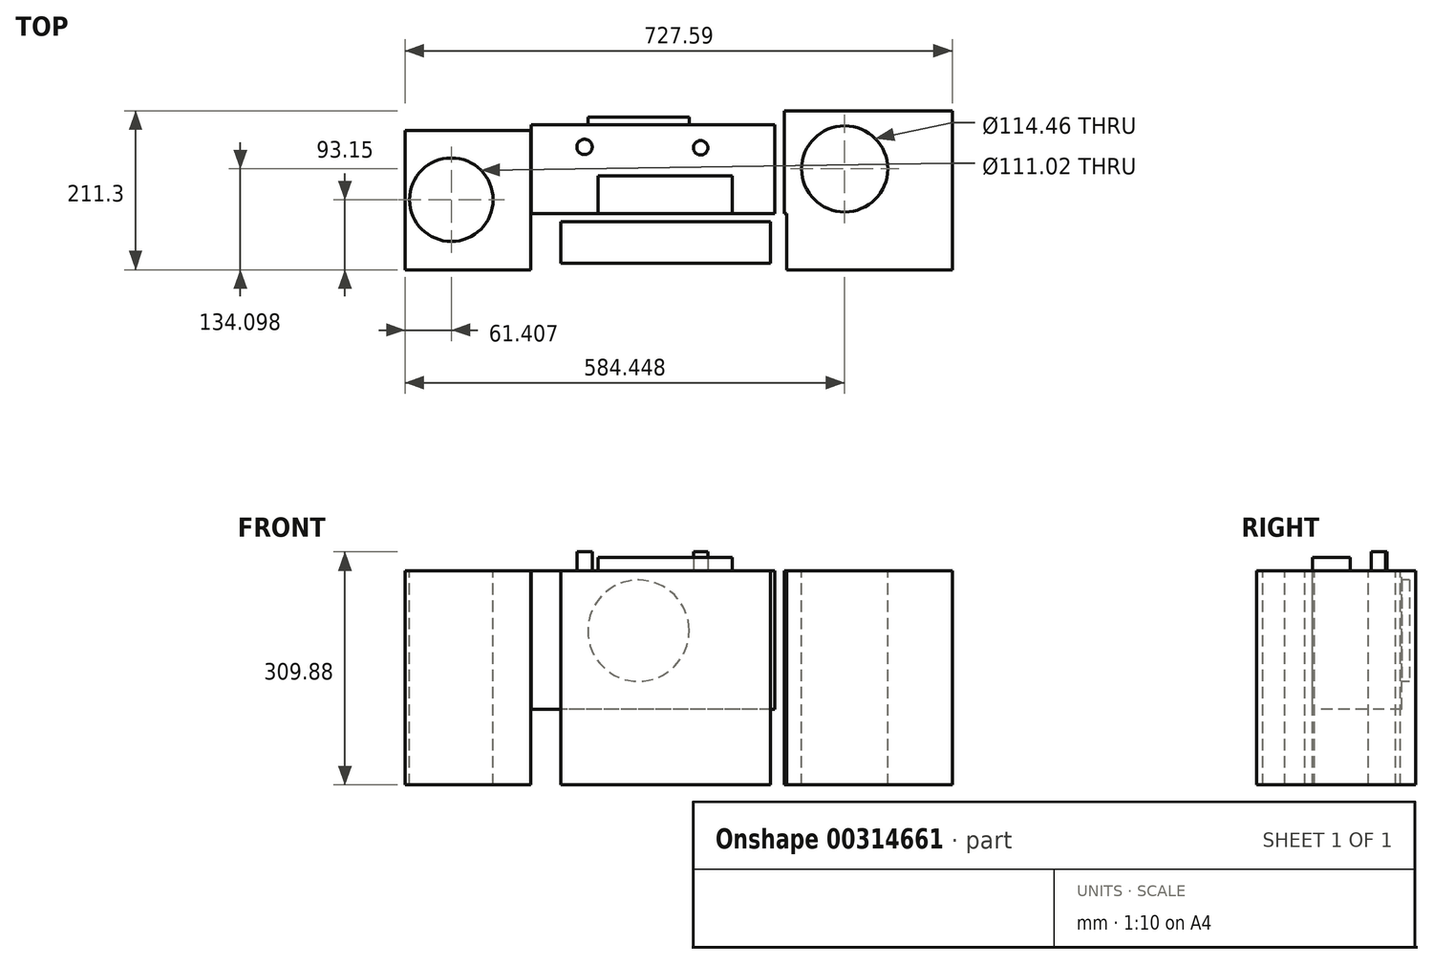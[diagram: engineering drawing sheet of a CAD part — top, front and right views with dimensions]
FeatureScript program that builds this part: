
annotation { "Feature Type Name" : "Feature", "Feature Type Description" : "" }
export const myFeature = defineFeature(function(context is Context, id is Id, definition is map)
    precondition{}
    {
        {
            var Q0;
            Q0=qCreatedBy(makeId("Top.planeOp"),FACE);
            var sketch = newSketch(context, id + "F0", { "sketchPlane" : qUnion([Q0])});
            skLineSegment(sketch, "E0.bottom", {"start": v(-134.95, 54.2) * mm, "end": v(69.6, 54.2) * mm});
            skLineSegment(sketch, "E0.top", {"start": v(-134.95, 26.65) * mm, "end": v(69.6, 26.65) * mm});
            skLineSegment(sketch, "E0.left", {"start": v(-134.95, 54.2) * mm, "end": v(-134.95, 26.65) * mm});
            skLineSegment(sketch, "E0.right", {"start": v(69.6, 54.2) * mm, "end": v(69.6, 26.65) * mm});
            skLineSegment(sketch, "E1.bottom", {"start": v(69.6, -77.72) * mm, "end": v(-134.95, -77.72) * mm});
            skLineSegment(sketch, "E1.top", {"start": v(69.6, 26.65) * mm, "end": v(-134.95, 26.65) * mm});
            skLineSegment(sketch, "E1.left", {"start": v(69.6, -77.72) * mm, "end": v(69.6, 26.65) * mm});
            skLineSegment(sketch, "E1.right", {"start": v(-134.95, -77.72) * mm, "end": v(-134.95, 26.65) * mm});
            skLineSegment(sketch, "E2.top", {"start": v(-134.95, 85.93) * mm, "end": v(69.6, 85.93) * mm});
            skLineSegment(sketch, "E2.left", {"start": v(-134.95, 54.2) * mm, "end": v(-134.95, 85.93) * mm});
            skLineSegment(sketch, "E2.right", {"start": v(69.6, 54.2) * mm, "end": v(69.6, 85.93) * mm});
            skSolve(sketch);
        }
        {
            var Q0;
            Q0=makeQuery(id+"F0.imprint","IMPRINT",FACE,{"disambiguationData":[TD([[makeQuery(id+"F0.imprint","IMPRINT",EDGE,{"derivedFrom":sQuery(id+"F0.wireOp",EDGE,"E0.bottom")}),1.0]])]});
            extrude(context, id + "F1", {"entities" : qUnion([Q0]), "depth" : 57.4 * mm});
        }
        {
            var Q0;
            Q0=makeQuery(id+"F1.opExtrude","CAP_FACE",FACE,{"disambiguationData":[OSD([sQuery(id+"F0.wireOp",EDGE,"E0.bottom"),sQuery(id+"F0.wireOp",EDGE,"E2.top"),sQuery(id+"F0.wireOp",EDGE,"E2.left"),sQuery(id+"F0.wireOp",EDGE,"E2.right")])],"isStart":false});
            var sketch = newSketch(context, id + "F2", { "sketchPlane" : qUnion([Q0])});
            skCircle(sketch, "E3", {"center": v(-110.98, 70.21) * mm, "radius": 10.18 * mm});
            skCircle(sketch, "E4", {"center": v(43.42, 69.05) * mm, "radius": 9.58 * mm});
            skSolve(sketch);
        }
        {
            var Q0;
            Q0 = qSketchRegion(id + "F2", true);
            extrude(context, id + "F3", {"entities" : qUnion([Q0]), "operationType" : NewBodyOperationType.ADD, "depth" : 25.4 * mm});
        }
        {
            var Q0;
            Q0=makeQuery(id+"F1.opExtrude","CAP_FACE",FACE,{"disambiguationData":[OSD([sQuery(id+"F0.wireOp",EDGE,"E0.bottom"),sQuery(id+"F0.wireOp",EDGE,"E2.top"),sQuery(id+"F0.wireOp",EDGE,"E2.left"),sQuery(id+"F0.wireOp",EDGE,"E2.right")])],"isStart":false});
            var sketch = newSketch(context, id + "F4", { "sketchPlane" : qUnion([Q0])});
            skLineSegment(sketch, "E5.bottom", {"start": v(142.11, 99.6) * mm, "end": v(-181.77, 99.6) * mm});
            skLineSegment(sketch, "E5.top", {"start": v(142.11, -18.76) * mm, "end": v(-181.77, -18.76) * mm});
            skLineSegment(sketch, "E5.left", {"start": v(142.11, 99.6) * mm, "end": v(142.11, -18.76) * mm});
            skLineSegment(sketch, "E5.right", {"start": v(-181.77, 99.6) * mm, "end": v(-181.77, -18.76) * mm});
            skSolve(sketch);
        }
        {
            var Q0;
            Q0 = qSketchRegion(id + "F4", true);
            extrude(context, id + "F5", {"entities" : qUnion([Q0]), "operationType" : NewBodyOperationType.ADD, "oppositeDirection" : true, "depth" : 183.9 * mm});
        }
        {
            var Q0;
            Q0=makeQuery(id+"F5.boolean.opBoolean","MERGE",FACE,{"derivedFrom":[makeQuery(id+"F1.opExtrude","CAP_FACE",FACE,{"disambiguationData":[OSD([sQuery(id+"F0.wireOp",EDGE,"E0.bottom"),sQuery(id+"F0.wireOp",EDGE,"E2.top"),sQuery(id+"F0.wireOp",EDGE,"E2.left"),sQuery(id+"F0.wireOp",EDGE,"E2.right")])],"isStart":false}),makeQuery(id+"F5.opExtrude","CAP_FACE",FACE,{"disambiguationData":[OSD([sQuery(id+"F4.wireOp",EDGE,"E5.bottom"),sQuery(id+"F4.wireOp",EDGE,"E5.top"),sQuery(id+"F4.wireOp",EDGE,"E5.left"),sQuery(id+"F4.wireOp",EDGE,"E5.right")])],"isStart":true})]});
            var sketch = newSketch(context, id + "F6", { "sketchPlane" : qUnion([Q0])});
            skLineSegment(sketch, "E6.bottom", {"start": v(-181.77, -18.76) * mm, "end": v(157.97, -18.76) * mm});
            skLineSegment(sketch, "E6.top", {"start": v(-181.77, -93.15) * mm, "end": v(157.97, -93.15) * mm});
            skLineSegment(sketch, "E6.left", {"start": v(-181.77, -18.76) * mm, "end": v(-181.77, -93.15) * mm});
            skLineSegment(sketch, "E6.right", {"start": v(157.97, -18.76) * mm, "end": v(157.97, -93.15) * mm});
            skLineSegment(sketch, "E7.bottom", {"start": v(378.03, 118.15) * mm, "end": v(154.83, 118.15) * mm});
            skLineSegment(sketch, "E7.top", {"start": v(378.03, -93.15) * mm, "end": v(154.83, -93.15) * mm});
            skLineSegment(sketch, "E7.left", {"start": v(378.03, 118.15) * mm, "end": v(378.03, -93.15) * mm});
            skLineSegment(sketch, "E7.right", {"start": v(154.83, 118.15) * mm, "end": v(154.83, -93.15) * mm});
            skLineSegment(sketch, "E8.bottom", {"start": v(-182.47, -93.15) * mm, "end": v(-349.56, -93.15) * mm});
            skLineSegment(sketch, "E8.top", {"start": v(-182.47, 91.81) * mm, "end": v(-349.56, 91.81) * mm});
            skLineSegment(sketch, "E8.left", {"start": v(-182.47, -93.15) * mm, "end": v(-182.47, 91.81) * mm});
            skLineSegment(sketch, "E8.right", {"start": v(-349.56, -93.15) * mm, "end": v(-349.56, 91.81) * mm});
            skCircle(sketch, "E9", {"center": v(234.89, 40.95) * mm, "radius": 57.23 * mm});
            skCircle(sketch, "E10", {"center": v(-288.15, 0) * mm, "radius": 55.5 * mm});
            skSolve(sketch);
        }
        {
            var Q0;
            {var subQ1=sQuery(id+"F6.wireOp",EDGE,"E6.top");Q0=makeQuery(id+"F6.imprint","IMPRINT",FACE,{"disambiguationData":[TD([[makeQuery(id+"F6.imprint","IMPRINT",EDGE,{"derivedFrom":subQ1}),1.0]])]});}
            var sketch = newSketch(context, id + "F7", { "sketchPlane" : qUnion([Q0])});
            skLineSegment(sketch, "E11.bottom", {"start": v(-142.37, -29.22) * mm, "end": v(136.37, -29.22) * mm});
            skLineSegment(sketch, "E11.top", {"start": v(-142.37, -84.8) * mm, "end": v(136.37, -84.8) * mm});
            skLineSegment(sketch, "E11.left", {"start": v(-142.37, -29.22) * mm, "end": v(-142.37, -84.8) * mm});
            skLineSegment(sketch, "E11.right", {"start": v(136.37, -29.22) * mm, "end": v(136.37, -84.8) * mm});
            skSolve(sketch);
        }
        {
            var Q0;
            Q0 = qSketchRegion(id + "F7", true);
            var Q1;
            {var subQ1=sQuery(id+"F6.wireOp",EDGE,"E6.right");Q1=makeQuery(id+"F6.imprint","IMPRINT",FACE,{"disambiguationData":[TD([[makeQuery(id+"F6.imprint","IMPRINT",EDGE,{"derivedFrom":subQ1}),1.0]])]});}
            var Q2;
            Q2=makeQuery(id+"F6.imprint","IMPRINT",FACE,{"disambiguationData":[TD([[makeQuery(id+"F6.imprint","IMPRINT",EDGE,{"derivedFrom":sQuery(id+"F6.wireOp",EDGE,"E8.bottom")}),-1.0]])]});
            extrude(context, id + "F8", {"entities" : qUnion([Q0, Q1, Q2]), "oppositeDirection" : true, "depth" : 284.48 * mm});
        }
        {
            var Q0;
            Q0=makeQuery(id+"F5.opExtrude","SWEPT_FACE",FACE,{"disambiguationData":[OSD([sQuery(id+"F4.wireOp",EDGE,"E5.bottom")])]});
            var sketch = newSketch(context, id + "F9", { "sketchPlane" : qUnion([Q0])});
            skCircle(sketch, "E12", {"center": v(39.3, -22.17) * mm, "radius": 67.36 * mm});
            skSolve(sketch);
        }
        {
            var Q0;
            Q0 = qSketchRegion(id + "F9", true);
            extrude(context, id + "F10", {"entities" : qUnion([Q0]), "operationType" : NewBodyOperationType.ADD, "depth" : 10.16 * mm});
        }
        {
            var Q0;
            Q0=makeQuery(id+"F5.boolean.opBoolean","MERGE",FACE,{"derivedFrom":[makeQuery(id+"F1.opExtrude","CAP_FACE",FACE,{"disambiguationData":[OSD([sQuery(id+"F0.wireOp",EDGE,"E0.bottom"),sQuery(id+"F0.wireOp",EDGE,"E2.top"),sQuery(id+"F0.wireOp",EDGE,"E2.left"),sQuery(id+"F0.wireOp",EDGE,"E2.right")])],"isStart":false}),makeQuery(id+"F5.opExtrude","CAP_FACE",FACE,{"disambiguationData":[OSD([sQuery(id+"F4.wireOp",EDGE,"E5.bottom"),sQuery(id+"F4.wireOp",EDGE,"E5.top"),sQuery(id+"F4.wireOp",EDGE,"E5.left"),sQuery(id+"F4.wireOp",EDGE,"E5.right")])],"isStart":true})]});
            var sketch = newSketch(context, id + "F11", { "sketchPlane" : qUnion([Q0])});
            skLineSegment(sketch, "E13.bottom", {"start": v(-92.86, 31.5) * mm, "end": v(85.22, 31.5) * mm});
            skLineSegment(sketch, "E13.top", {"start": v(-92.86, -18.76) * mm, "end": v(85.22, -18.76) * mm});
            skLineSegment(sketch, "E13.left", {"start": v(-92.86, 31.5) * mm, "end": v(-92.86, -18.76) * mm});
            skLineSegment(sketch, "E13.right", {"start": v(85.22, 31.5) * mm, "end": v(85.22, -18.76) * mm});
            skSolve(sketch);
        }
        {
            var Q0;
            Q0 = qSketchRegion(id + "F11", true);
            extrude(context, id + "F12", {"entities" : qUnion([Q0]), "operationType" : NewBodyOperationType.ADD, "depth" : 17.78 * mm});
        }
    });
